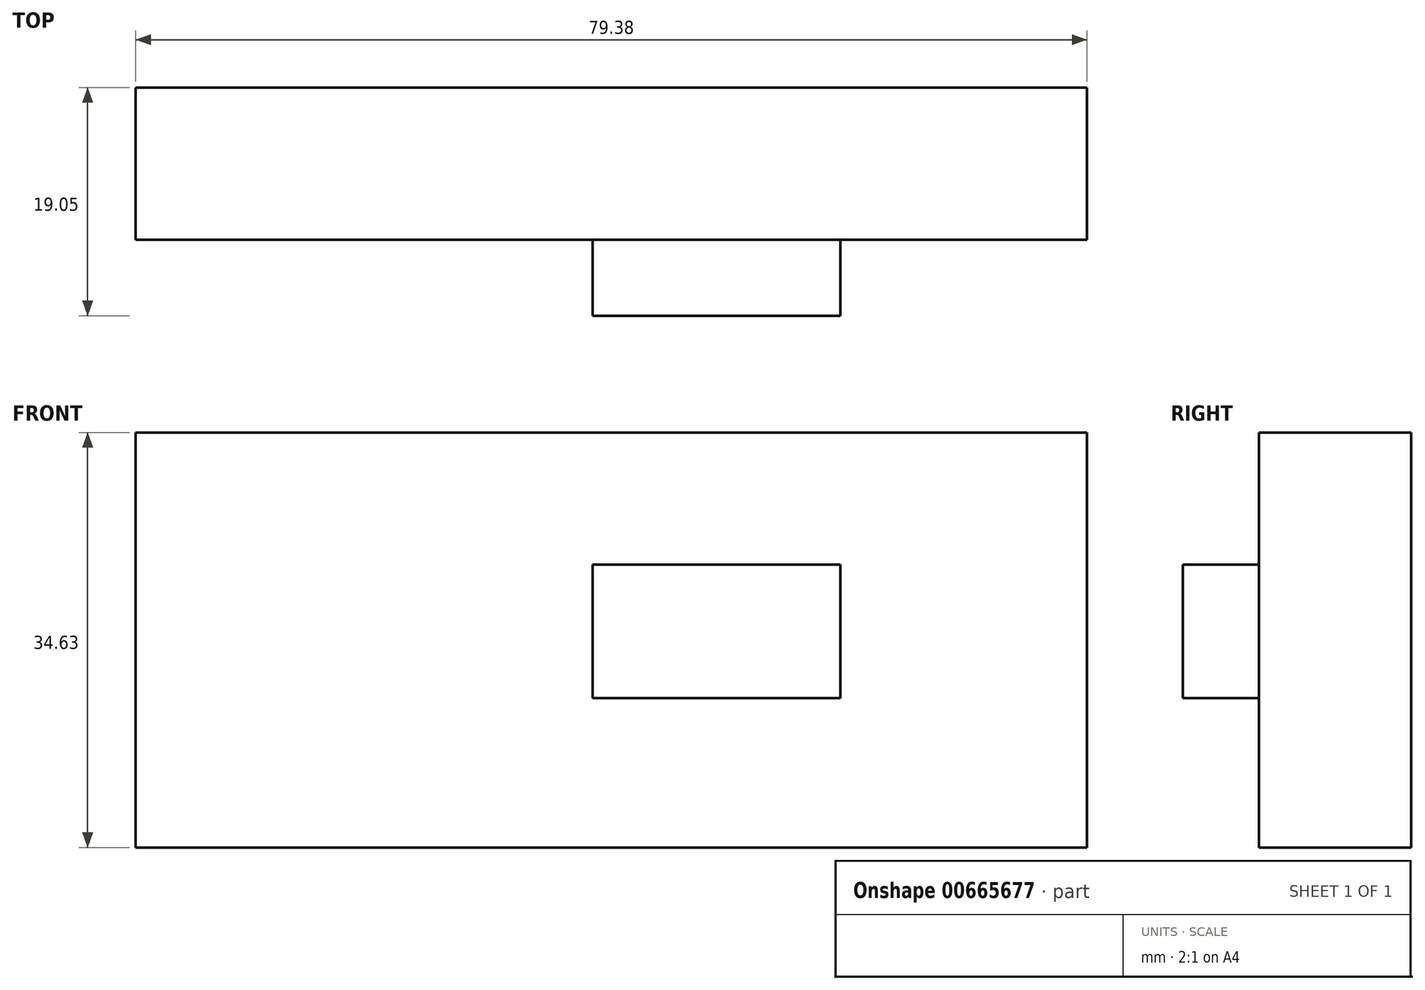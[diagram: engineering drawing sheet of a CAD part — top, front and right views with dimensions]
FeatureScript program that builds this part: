
annotation { "Feature Type Name" : "Feature", "Feature Type Description" : "" }
export const myFeature = defineFeature(function(context is Context, id is Id, definition is map)
    precondition{}
    {
        {
            var Q0;
            Q0=qCreatedBy(makeId("Front.planeOp"),FACE);
            var sketch = newSketch(context, id + "F0", { "sketchPlane" : qUnion([Q0])});
            skLineSegment(sketch, "E0.bottom", {"start": v(-38.1, 22.18) * mm, "end": v(41.27, 22.18) * mm});
            skLineSegment(sketch, "E0.top", {"start": v(-38.1, -12.45) * mm, "end": v(41.27, -12.45) * mm});
            skLineSegment(sketch, "E0.left", {"start": v(-38.1, 22.18) * mm, "end": v(-38.1, -12.45) * mm});
            skLineSegment(sketch, "E0.right", {"start": v(41.27, 22.18) * mm, "end": v(41.27, -12.45) * mm});
            skSolve(sketch);
        }
        {
            var Q0;
            Q0 = qSketchRegion(id + "F0", true);
            extrude(context, id + "F1", {"entities" : qUnion([Q0]), "depth" : 12.7 * mm, "offsetDistance" : 25.4 * mm});
        }
        {
            var Q0;
            Q0=makeQuery(id+"F1.opExtrude","CAP_FACE",FACE,{"disambiguationData":[OSD([sQuery(id+"F0.wireOp",EDGE,"E0.bottom"),sQuery(id+"F0.wireOp",EDGE,"E0.top"),sQuery(id+"F0.wireOp",EDGE,"E0.left"),sQuery(id+"F0.wireOp",EDGE,"E0.right")])],"isStart":false});
            var sketch = newSketch(context, id + "F2", { "sketchPlane" : qUnion([Q0])});
            skLineSegment(sketch, "E1.bottom", {"start": v(0, 0) * mm, "end": v(20.69, 0) * mm});
            skLineSegment(sketch, "E1.top", {"start": v(0, 11.16) * mm, "end": v(20.69, 11.16) * mm});
            skLineSegment(sketch, "E1.left", {"start": v(0, 0) * mm, "end": v(0, 11.16) * mm});
            skLineSegment(sketch, "E1.right", {"start": v(20.69, 0) * mm, "end": v(20.69, 11.16) * mm});
            skSolve(sketch);
        }
        {
            var Q0;
            Q0=makeQuery(id+"F2.imprint","IMPRINT",FACE,{"disambiguationData":[TD([[makeQuery(id+"F2.imprint","IMPRINT",EDGE,{"derivedFrom":sQuery(id+"F2.wireOp",EDGE,"E1.bottom")}),1.0]])]});
            extrude(context, id + "F3", {"entities" : qUnion([Q0]), "operationType" : NewBodyOperationType.ADD, "depth" : 6.35 * mm, "offsetDistance" : 25.4 * mm});
        }
    });
